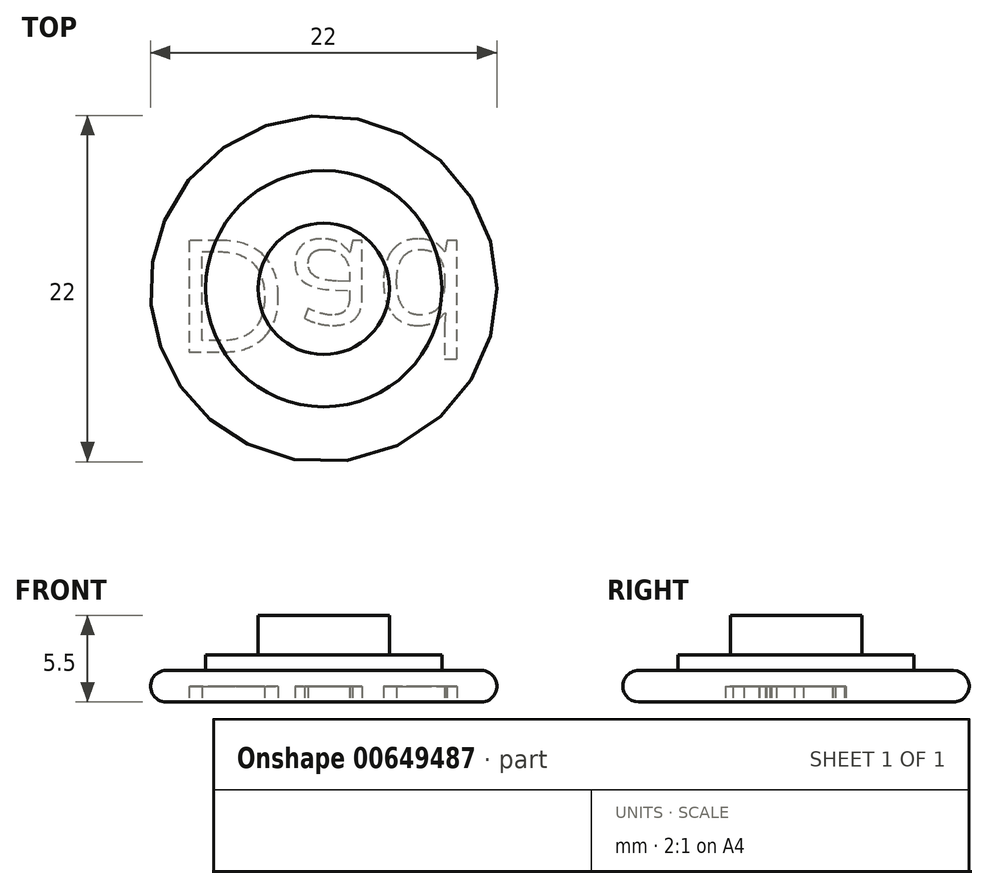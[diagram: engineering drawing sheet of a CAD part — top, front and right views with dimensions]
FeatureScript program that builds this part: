
annotation { "Feature Type Name" : "Feature", "Feature Type Description" : "" }
export const myFeature = defineFeature(function(context is Context, id is Id, definition is map)
    precondition{}
    {
        {
            var Q0;
            Q0=qCreatedBy(makeId("Top.planeOp"),FACE);
            var sketch = newSketch(context, id + "F0", { "sketchPlane" : qUnion([Q0])});
            skCircle(sketch, "E0", {"center": v(0, 0) * mm, "radius": 11 * mm});
            skCircle(sketch, "E1", {"center": v(0, 0) * mm, "radius": 7.5 * mm});
            skCircle(sketch, "E2", {"center": v(0, 0) * mm, "radius": 4.17 * mm});
            skSolve(sketch);
        }
        {
            var Q0;
            Q0=makeQuery(id+"F0.imprint","IMPRINT",FACE,{"disambiguationData":[TD([[makeQuery(id+"F0.imprint","IMPRINT",EDGE,{"derivedFrom":sQuery(id+"F0.wireOp",EDGE,"E0")}),1.0]])]});
            extrude(context, id + "F1", {"entities" : qUnion([Q0]), "depth" : 2 * mm, "offsetDistance" : 25 * mm});
        }
        {
            var Q0;
            Q0=makeQuery(id+"F0.imprint","IMPRINT",FACE,{"disambiguationData":[TD([[makeQuery(id+"F0.imprint","IMPRINT",EDGE,{"derivedFrom":sQuery(id+"F0.wireOp",EDGE,"E1")}),1.0]])]});
            extrude(context, id + "F2", {"entities" : qUnion([Q0]), "operationType" : NewBodyOperationType.ADD, "depth" : 3 * mm, "offsetDistance" : 25 * mm});
        }
        {
            var Q0;
            Q0=makeQuery(id+"F0.imprint","IMPRINT",FACE,{"disambiguationData":[TD([[makeQuery(id+"F0.imprint","IMPRINT",EDGE,{"derivedFrom":sQuery(id+"F0.wireOp",EDGE,"E2")}),1.0]])]});
            extrude(context, id + "F3", {"entities" : qUnion([Q0]), "operationType" : NewBodyOperationType.ADD, "depth" : 5.5 * mm, "offsetDistance" : 25 * mm});
        }
        {
            var Q0;
            Q0=makeQuery(id+"F1.opExtrude","CAP_EDGE",EDGE,{"disambiguationData":[OSD([sQuery(id+"F0.wireOp",EDGE,"E0")])],"isStart":false});
            var Q1;
            Q1=makeQuery(id+"F1.opExtrude","CAP_EDGE",EDGE,{"disambiguationData":[OSD([sQuery(id+"F0.wireOp",EDGE,"E0")])],"isStart":true});
            fillet(context, id + "F4", {"entities" : qUnion([Q0, Q1]), "radius" : 1 * mm, "tangentPropagation" : true, "allowEdgeOverflow" : false});
        }
        {
            var Q0;
            {var subQ0=sQuery(id+"F0.wireOp",EDGE,"E2");var subQ1=sQuery(id+"F0.wireOp",EDGE,"E1");Q0=makeQuery(id+"F3.boolean.opBoolean","MERGE",FACE,{"derivedFrom":[makeQuery(id+"F2.boolean.opBoolean","MERGE",FACE,{"derivedFrom":[makeQuery(id+"F1.opExtrude","CAP_FACE",FACE,{"disambiguationData":[OSD([sQuery(id+"F0.wireOp",EDGE,"E0"),subQ1])],"isStart":true}),makeQuery(id+"F2.opExtrude","CAP_FACE",FACE,{"disambiguationData":[OSD([subQ1,subQ0])],"isStart":true})]}),makeQuery(id+"F3.opExtrude","CAP_FACE",FACE,{"disambiguationData":[OSD([subQ0])],"isStart":true})]});}
            var sketch = newSketch(context, id + "F5", { "sketchPlane" : qUnion([Q0])});
            skText(sketch, "E3", { "text": "Dad", "fontName": "OpenSans-Regular.ttf"});
            const initialGuessF5  = {"E3": [-0.00952, -0.00307, 1, 0, 0.00715]};
            skSetInitialGuess(sketch, initialGuessF5);
            skSolve(sketch);
        }
        {
            var Q0;
            Q0 = qSketchRegion(id + "F5", true);
            extrude(context, id + "F6", {"entities" : qUnion([Q0]), "operationType" : NewBodyOperationType.REMOVE, "oppositeDirection" : true, "depth" : 1 * mm, "offsetDistance" : 25 * mm});
        }
    });
